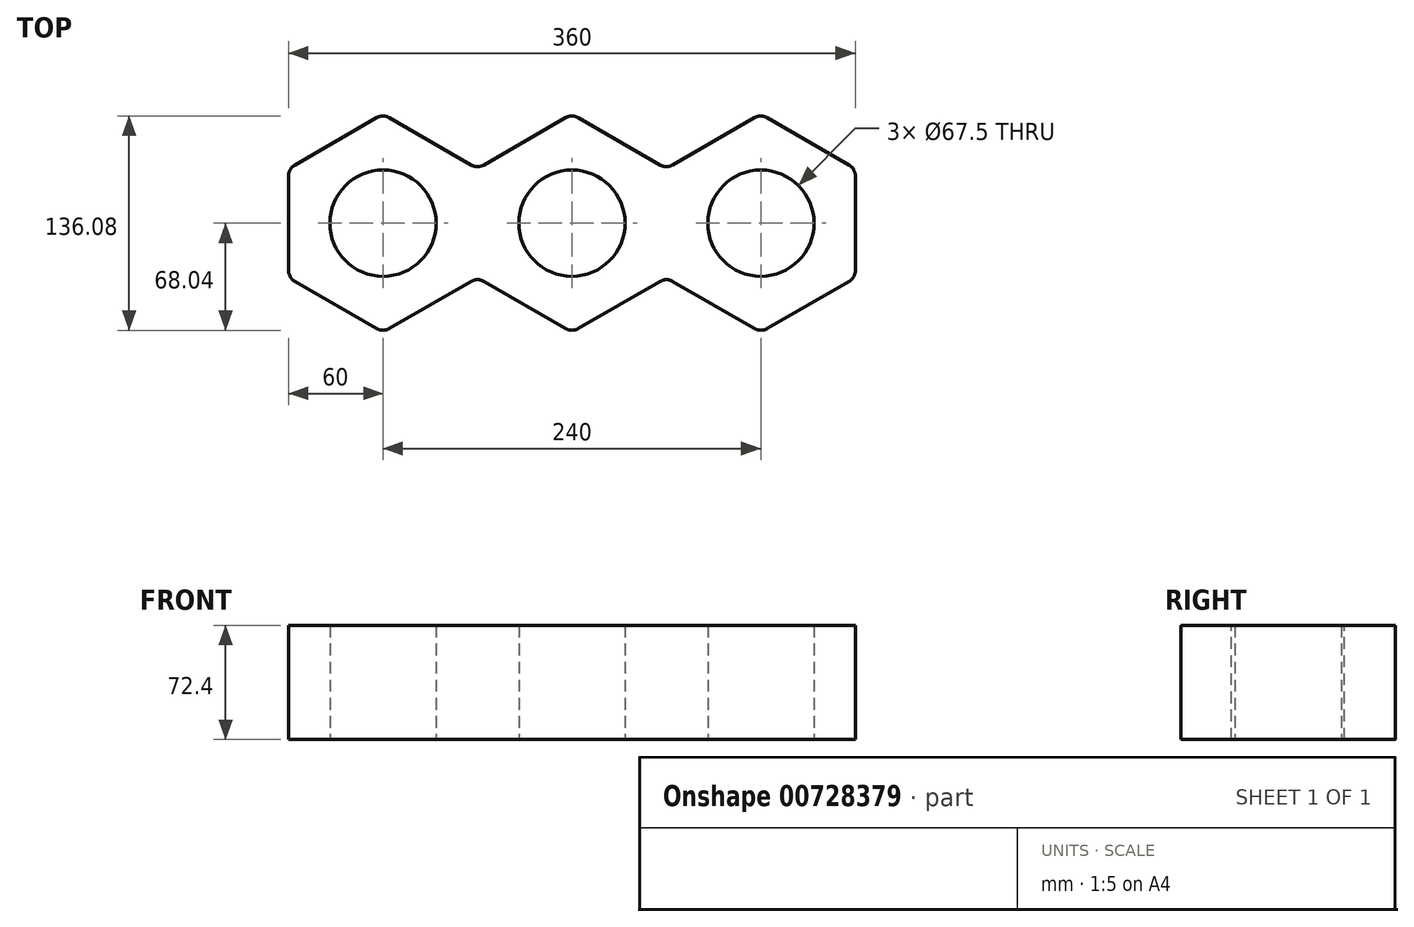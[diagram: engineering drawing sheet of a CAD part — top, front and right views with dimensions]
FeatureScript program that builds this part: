
annotation { "Feature Type Name" : "Feature", "Feature Type Description" : "" }
export const myFeature = defineFeature(function(context is Context, id is Id, definition is map)
    precondition{}
    {
        {
            var Q0;
            Q0=qCreatedBy(makeId("Top.planeOp"),FACE);
            var sketch = newSketch(context, id + "F0", { "sketchPlane" : qUnion([Q0])});
            skCircle(sketch, "E0", {"center": v(0, 0) * mm, "radius": 33.75 * mm});
            skLineSegment(sketch, "E1", {"start": v(0, 0) * mm, "end": v(16.88, -29.23) * mm, "construction": true});
            skCircle(sketch, "E2.cCircle", {"center": v(0, 0) * mm, "radius": 60 * mm, "construction": true});
            skLineSegment(sketch, "E2.0", {"start": v(60, -34.64) * mm, "end": v(0, -69.28) * mm});
            skLineSegment(sketch, "E2.1", {"start": v(0, -69.28) * mm, "end": v(-60, -34.64) * mm});
            skLineSegment(sketch, "E2.2", {"start": v(-60, -34.64) * mm, "end": v(-60, 34.64) * mm});
            skLineSegment(sketch, "E2.3", {"start": v(-60, 34.64) * mm, "end": v(0, 69.28) * mm});
            skLineSegment(sketch, "E2.4", {"start": v(0, 69.28) * mm, "end": v(60, 34.64) * mm});
            skLineSegment(sketch, "E2.5", {"start": v(60, 34.64) * mm, "end": v(60, -34.64) * mm});
            skPoint(sketch, "E2.0.midPoint", {"position": v(30, -51.96) * mm});
            skLineSegment(sketch, "E3", {"start": v(0, 0) * mm, "end": v(120, 0) * mm, "construction": true});
            skCircle(sketch, "E4", {"center": v(120, 0) * mm, "radius": 33.75 * mm});
            skCircle(sketch, "E5.cCircle", {"center": v(120, 0) * mm, "radius": 60 * mm, "construction": true});
            skLineSegment(sketch, "E5.0", {"start": v(60, -34.64) * mm, "end": v(60, 34.64) * mm});
            skLineSegment(sketch, "E5.1", {"start": v(60, 34.64) * mm, "end": v(120, 69.28) * mm});
            skLineSegment(sketch, "E5.2", {"start": v(120, 69.28) * mm, "end": v(180, 34.64) * mm});
            skLineSegment(sketch, "E5.3", {"start": v(180, 34.64) * mm, "end": v(180, -34.64) * mm});
            skLineSegment(sketch, "E5.4", {"start": v(180, -34.64) * mm, "end": v(120, -69.28) * mm});
            skLineSegment(sketch, "E5.5", {"start": v(120, -69.28) * mm, "end": v(60, -34.64) * mm});
            skPoint(sketch, "E5.0.midPoint", {"position": v(60, 0) * mm});
            skLineSegment(sketch, "E6", {"start": v(120, 0) * mm, "end": v(240, 0) * mm, "construction": true});
            skPoint(sketch, "E6.endSnap0", {"position": v(180, 0) * mm});
            skCircle(sketch, "E7", {"center": v(240, 0) * mm, "radius": 33.75 * mm});
            skLineSegment(sketch, "E8", {"start": v(240, 0) * mm, "end": v(401.6, 0) * mm, "construction": true});
            skCircle(sketch, "E9.cCircle", {"center": v(240, 0) * mm, "radius": 60 * mm, "construction": true});
            skLineSegment(sketch, "E9.0", {"start": v(300, 34.64) * mm, "end": v(300, -34.64) * mm});
            skLineSegment(sketch, "E9.1", {"start": v(300, -34.64) * mm, "end": v(240, -69.28) * mm});
            skLineSegment(sketch, "E9.2", {"start": v(240, -69.28) * mm, "end": v(180, -34.64) * mm});
            skLineSegment(sketch, "E9.3", {"start": v(180, -34.64) * mm, "end": v(180, 34.64) * mm});
            skLineSegment(sketch, "E9.4", {"start": v(180, 34.64) * mm, "end": v(240, 69.28) * mm});
            skLineSegment(sketch, "E9.5", {"start": v(240, 69.28) * mm, "end": v(300, 34.64) * mm});
            skPoint(sketch, "E9.0.midPoint", {"position": v(300, 0) * mm});
            skSolve(sketch);
        }
        {
            var Q0;
            Q0=makeQuery(id+"F0.imprint","IMPRINT",FACE,{"disambiguationData":[TD([[makeQuery(id+"F0.imprint","IMPRINT",EDGE,{"derivedFrom":sQuery(id+"F0.wireOp",EDGE,"E0")}),-1.0]])]});
            var Q1;
            Q1=makeQuery(id+"F0.imprint","IMPRINT",FACE,{"disambiguationData":[TD([[makeQuery(id+"F0.imprint","IMPRINT",EDGE,{"derivedFrom":sQuery(id+"F0.wireOp",EDGE,"E4")}),-1.0]])]});
            var Q2;
            Q2=makeQuery(id+"F0.imprint","IMPRINT",FACE,{"disambiguationData":[TD([[makeQuery(id+"F0.imprint","IMPRINT",EDGE,{"derivedFrom":sQuery(id+"F0.wireOp",EDGE,"E7")}),-1.0]])]});
            extrude(context, id + "F1", {"entities" : qUnion([Q0, Q1, Q2]), "depth" : 72.4 * mm, "offsetDistance" : 25 * mm});
        }
        {
            var Q0;
            Q0=makeQuery(id+"F1.opExtrude","SWEPT_EDGE",EDGE,{"disambiguationData":[OSD([sQuery(id+"F0.wireOp",EDGE,"E2.0"),sQuery(id+"F0.wireOp",EDGE,"E5.0"),sQuery(id+"F0.wireOp",EDGE,"E5.5")])]});
            var Q1;
            Q1=makeQuery(id+"F1.opExtrude","SWEPT_EDGE",EDGE,{"disambiguationData":[OSD([sQuery(id+"F0.wireOp",EDGE,"E2.0"),sQuery(id+"F0.wireOp",EDGE,"E2.1")])]});
            var Q2;
            Q2=makeQuery(id+"F1.opExtrude","SWEPT_EDGE",EDGE,{"disambiguationData":[OSD([sQuery(id+"F0.wireOp",EDGE,"E2.1"),sQuery(id+"F0.wireOp",EDGE,"E2.2")])]});
            var Q3;
            Q3=makeQuery(id+"F1.opExtrude","SWEPT_EDGE",EDGE,{"disambiguationData":[OSD([sQuery(id+"F0.wireOp",EDGE,"E5.4"),sQuery(id+"F0.wireOp",EDGE,"E5.5")])]});
            var Q4;
            Q4=makeQuery(id+"F1.opExtrude","SWEPT_EDGE",EDGE,{"disambiguationData":[OSD([sQuery(id+"F0.wireOp",EDGE,"E5.3"),sQuery(id+"F0.wireOp",EDGE,"E5.4")])]});
            var Q5;
            Q5=makeQuery(id+"F1.opExtrude","SWEPT_EDGE",EDGE,{"disambiguationData":[OSD([sQuery(id+"F0.wireOp",EDGE,"E5.2"),sQuery(id+"F0.wireOp",EDGE,"E5.3")])]});
            var Q6;
            Q6=makeQuery(id+"F1.opExtrude","SWEPT_EDGE",EDGE,{"disambiguationData":[OSD([sQuery(id+"F0.wireOp",EDGE,"E5.1"),sQuery(id+"F0.wireOp",EDGE,"E5.2")])]});
            var Q7;
            Q7=makeQuery(id+"F1.opExtrude","SWEPT_EDGE",EDGE,{"disambiguationData":[OSD([sQuery(id+"F0.wireOp",EDGE,"E2.3"),sQuery(id+"F0.wireOp",EDGE,"E2.4")])]});
            var Q8;
            Q8=makeQuery(id+"F1.opExtrude","SWEPT_EDGE",EDGE,{"disambiguationData":[OSD([sQuery(id+"F0.wireOp",EDGE,"E2.4"),sQuery(id+"F0.wireOp",EDGE,"E5.0"),sQuery(id+"F0.wireOp",EDGE,"E5.1")])]});
            var Q9;
            Q9=makeQuery(id+"F1.opExtrude","SWEPT_EDGE",EDGE,{"disambiguationData":[OSD([sQuery(id+"F0.wireOp",EDGE,"E2.2"),sQuery(id+"F0.wireOp",EDGE,"E2.3")])]});
            var Q10;
            Q10=makeQuery(id+"F1.opExtrude","SWEPT_EDGE",EDGE,{"disambiguationData":[OSD([sQuery(id+"F0.wireOp",EDGE,"E5.4"),sQuery(id+"F0.wireOp",EDGE,"E9.2"),sQuery(id+"F0.wireOp",EDGE,"E9.3")])]});
            var Q11;
            Q11=makeQuery(id+"F1.opExtrude","SWEPT_EDGE",EDGE,{"disambiguationData":[OSD([sQuery(id+"F0.wireOp",EDGE,"E9.1"),sQuery(id+"F0.wireOp",EDGE,"E9.2")])]});
            var Q12;
            Q12=makeQuery(id+"F1.opExtrude","SWEPT_EDGE",EDGE,{"disambiguationData":[OSD([sQuery(id+"F0.wireOp",EDGE,"E9.0"),sQuery(id+"F0.wireOp",EDGE,"E9.1")])]});
            var Q13;
            Q13=makeQuery(id+"F1.opExtrude","SWEPT_EDGE",EDGE,{"disambiguationData":[OSD([sQuery(id+"F0.wireOp",EDGE,"E9.0"),sQuery(id+"F0.wireOp",EDGE,"E9.5")])]});
            var Q14;
            Q14=makeQuery(id+"F1.opExtrude","SWEPT_EDGE",EDGE,{"disambiguationData":[OSD([sQuery(id+"F0.wireOp",EDGE,"E9.4"),sQuery(id+"F0.wireOp",EDGE,"E9.5")])]});
            var Q15;
            Q15=makeQuery(id+"F1.opExtrude","SWEPT_EDGE",EDGE,{"disambiguationData":[OSD([sQuery(id+"F0.wireOp",EDGE,"E5.2"),sQuery(id+"F0.wireOp",EDGE,"E9.3"),sQuery(id+"F0.wireOp",EDGE,"E9.4")])]});
            fillet(context, id + "F2", {"entities" : qUnion([Q0, Q1, Q2, Q3, Q4, Q5, Q6, Q7, Q8, Q9, Q10, Q11, Q12, Q13, Q14, Q15]), "radius" : 8 * mm, "allowEdgeOverflow" : false});
        }
    });
